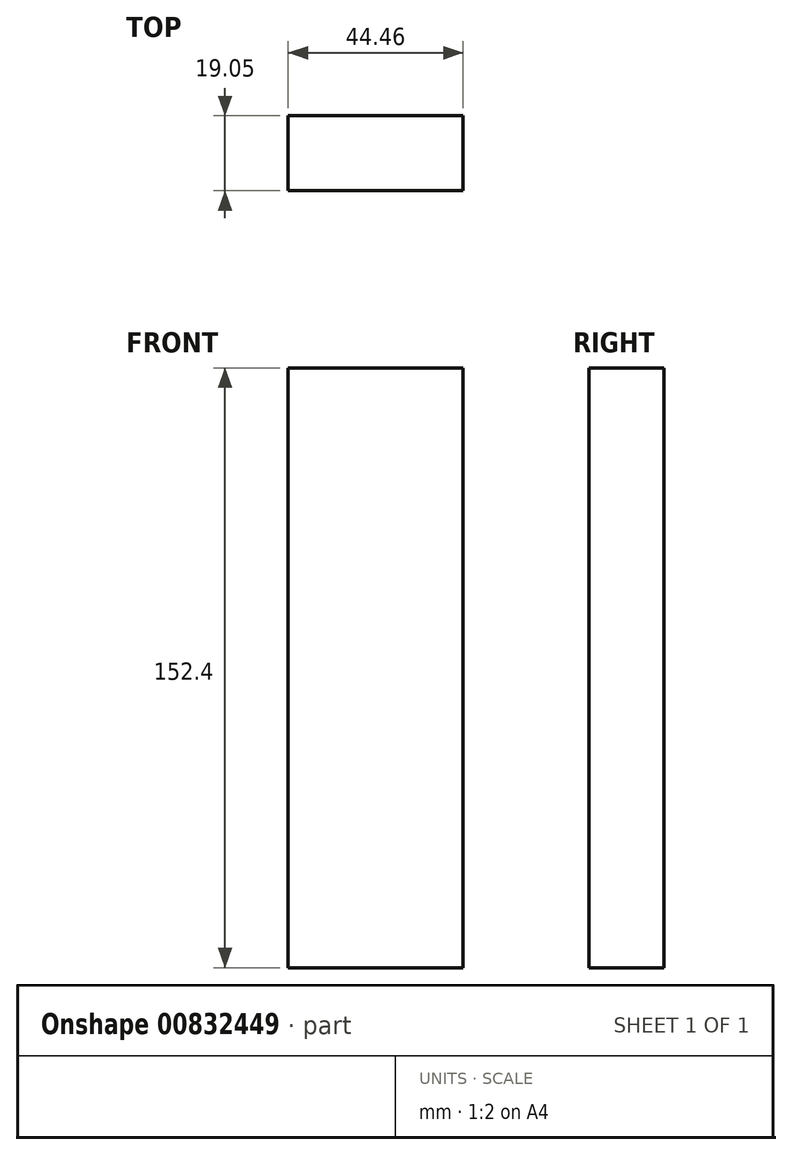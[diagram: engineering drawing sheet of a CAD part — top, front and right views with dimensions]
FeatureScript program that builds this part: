
annotation { "Feature Type Name" : "Feature", "Feature Type Description" : "" }
export const myFeature = defineFeature(function(context is Context, id is Id, definition is map)
    precondition{}
    {
        {
            var Q0;
            Q0=qCreatedBy(makeId("Front.planeOp"),FACE);
            var sketch = newSketch(context, id + "F0", { "sketchPlane" : qUnion([Q0])});
            skLineSegment(sketch, "E0.bottom", {"start": v(22.22, -76.2) * mm, "end": v(-22.23, -76.2) * mm});
            skLineSegment(sketch, "E0.top", {"start": v(22.22, 76.2) * mm, "end": v(-22.23, 76.2) * mm});
            skLineSegment(sketch, "E0.left", {"start": v(22.22, -76.2) * mm, "end": v(22.22, 76.2) * mm});
            skLineSegment(sketch, "E0.right", {"start": v(-22.23, -76.2) * mm, "end": v(-22.23, 76.2) * mm});
            skPoint(sketch, "E0.middle", {"position": v(0, 0) * mm});
            skSolve(sketch);
        }
        {
            var Q0;
            Q0=makeQuery(id+"F0.imprint","IMPRINT",FACE,{"disambiguationData":[TD([[makeQuery(id+"F0.imprint","IMPRINT",EDGE,{"derivedFrom":sQuery(id+"F0.wireOp",EDGE,"E0.bottom")}),-1.0]])]});
            extrude(context, id + "F1", {"entities" : qUnion([Q0]), "depth" : 19.05 * mm, "offsetDistance" : 25.4 * mm});
        }
    });
